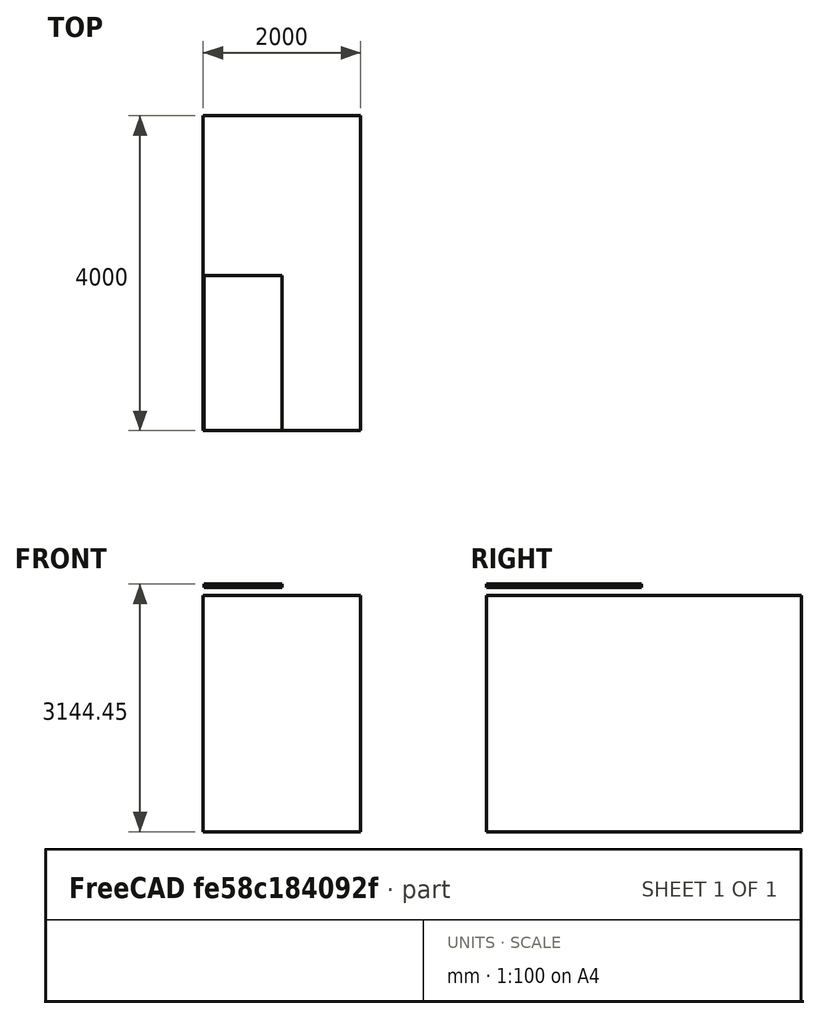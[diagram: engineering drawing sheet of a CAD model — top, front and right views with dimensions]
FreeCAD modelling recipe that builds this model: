
FCSTD DOCUMENT  (FreeCAD 0.19R)
Label: genesis-booth
License: Creative Commons Attribution-ShareAlike
LicenseURL: http://creativecommons.org/licenses/by-sa/4.0/
objects: Sketcher::SketchObject×6, Part::Part2DObjectPython×6, Part::Fuse×2, Spreadsheet::Sheet×1, Part::Feature×1, Part::FeaturePython×1, Part::Extrusion×1, App::DocumentObjectGroup×1
note: 16 computed .brp shape members not serialized (recipe doc carries the construction recipe); baked Part::Feature solids carry a one-line shape summary decoded from their .brp

FEATURE [Sketcher::SketchObject] Sketch  label="exterior walls sketch"
  FullyConstrained = true
  expr: Constraints[7] = Spreadsheet.building_length
  expr: Constraints[6] = Spreadsheet.building_width
  sketch-geometry (4):
    g0: LineSegment StartX=1000 StartY=2000 StartZ=0 EndX=1000 EndY=-2000 EndZ=0
    g1: LineSegment StartX=1000 StartY=-2000 StartZ=0 EndX=-1000 EndY=-2000 EndZ=0
    g2: LineSegment StartX=-1000 StartY=-2000 StartZ=0 EndX=-1000 EndY=2000 EndZ=0
    g3: LineSegment StartX=-1000 StartY=2000 StartZ=0 EndX=1000 EndY=2000 EndZ=0
  constraints (10):
    c: Coincident(g0,g1)
    c: Coincident(g1,g2)
    c: Coincident(g2,g3)
    c: Coincident(g0,g3)
    c: Vertical(g0)
    c: Horizontal(g1)
    c: Distance(g3) = 2000
    c: Distance(g0) = 4000
    c: Symmetric(g2,g1,g-1)
    c: Symmetric(g2,g0,g-2)
FEATURE [Sketcher::SketchObject] Sketch001  label="roof sketch"
  AttachmentOffset = pos=(0,0,3000) rot=(0,0,1;0rad)
  ExternalGeometry = -> [Sketch]
  FullyConstrained = true
  MapMode = 2
  Placement = pos=(0,0,3000) rot=(0,0,1;0rad)
  Support = -> [Sketch]
  expr: .AttachmentOffset.Base.z = Spreadsheet.building_height
  sketch-geometry (5):
    g0: LineSegment StartX=1000 StartY=2000 StartZ=0 EndX=1000 EndY=-2000 EndZ=0
    g1: LineSegment StartX=1000 StartY=-2000 StartZ=0 EndX=-1000 EndY=-2000 EndZ=0
    g2: LineSegment StartX=-1000 StartY=-2000 StartZ=0 EndX=-1000 EndY=2000 EndZ=0
    g3: LineSegment StartX=-1000 StartY=2000 StartZ=0 EndX=1000 EndY=2000 EndZ=0
    g4: LineSegment StartX=0 StartY=2000 StartZ=0 EndX=0 EndY=-2000 EndZ=0
  constraints (12):
    c: Coincident(g-6,g0)
    c: Coincident(g0,g-4)
    c: Coincident(g0,g1)
    c: Coincident(g1,g-5)
    c: Coincident(g1,g2)
    c: Coincident(g2,g-6)
    c: Coincident(g2,g3)
    c: Coincident(g3,g0)
    c: Vertical(g4)
    c: PointOnObject(g4,g-2)
    c: PointOnObject(g4,g3)
    c: PointOnObject(g4,g1)
FEATURE [Spreadsheet::Sheet] Spreadsheet
  cells = B1=Length; C1=Width; D1=Height; A2=Exterior Walls; B2(building_length)==4m; C2(building_width)==2m; D2(building_height)==3m; A3=Roof; C3(roof_overhang)==8m; D3(roof_height)==0.1m; A4=Roof Overhang; D4(roof_overhang_loss)==1.5m
FEATURE [Sketcher::SketchObject] Sketch002  label="roof ridge sketch"
  AttachmentOffset = pos=(0,0,100) rot=(0,0,1;0rad)
  ExternalGeometry = -> [Sketch001]
  FullyConstrained = true
  MapMode = 2
  Placement = pos=(0,0,3100) rot=(0,0,1;0rad)
  Support = -> [Sketch001]
  expr: .AttachmentOffset.Base.z = Spreadsheet.roof_height + 0m
  sketch-geometry (3):
    g0: LineSegment StartX=0 StartY=2000 StartZ=0 EndX=0 EndY=-2000 EndZ=0
    g1: LineSegment StartX=0 StartY=2000 StartZ=0 EndX=0 EndY=2500 EndZ=0
    g2: LineSegment StartX=0 StartY=-2000 StartZ=0 EndX=0 EndY=-2500 EndZ=0
  constraints (8):
    c: Coincident(g-3,g0)
    c: Coincident(g0,g-3)
    c: Coincident(g1,g0)
    c: PointOnObject(g1,g-2)
    c: Coincident(g2,g0)
    c: PointOnObject(g2,g-2)
    c: Distance(g1) = 500
    c: Equal(g1,g2)
FEATURE [Part::Part2DObjectPython] Wire001  # Draft 2D object (typed FeaturePython)
  Area = 4.01995e+06
  ChamferSize = 0
  Closed = true
  End = (4.4338e-12,2000,3100)
  FilletRadius = 0
  Length = 10010
  MakeFace = true
  Placement = pos=(-1000,2000,3000) rot=(0.754466,0.044251,0.654846;1.70074rad)
  Points = (4) [(0,0,0),(-2748.15,509.448,2861.49),(-2183.33,-24.0816,3498.93),(564.82,-533.53,637.436)]
  Start = (-1000,2000,3000)
  Subdivisions = 0
FEATURE [Part::Part2DObjectPython] Wire002  # Draft 2D object (typed FeaturePython)
  Area = 4.01995e+06
  ChamferSize = 0
  Closed = true
  End = (-4.3201e-12,2000,3100)
  FilletRadius = 0
  Length = 10010
  MakeFace = true
  Placement = pos=(0,-2000,3100) rot=(0.754466,0.044251,0.654846;1.70074rad)
  Points = (4) [(0,0,0),(461.981,-689.697,566.473),(3210.13,-1199.15,-2295.02),(2748.15,-509.448,-2861.49)]
  Start = (0,-2000,3100)
  Subdivisions = 0
FEATURE [Part::Fuse] Fusion  label="rooftop"
  Base = -> Wire002
  Tool = -> Wire001
FEATURE [Part::Feature] Part__Feature  label="PV Panel"
  Placement = pos=(-2293.4,-2787.4,-3250) rot=(0,0,1;0rad)
  shape: bbox 990.6 x 1969 x 44.45 mm, 6 faces (baked)
FEATURE [Part::FeaturePython] Array  label="PV Array"  # Draft array (typed FeaturePython)
  Angle = 360
  ArrayType = 0
  Axis = (0,0,1)
  Base = -> Part__Feature
  Center = (0,0,0)
  Count = 4
  ExpandArray = false
  Fuse = false
  IntervalAxis = (0,0,0)
  IntervalX = (1000,0,0)
  IntervalY = (0,2000,0)
  IntervalZ = (0,0,100)
  NumberCircles = 3
  NumberPolar = 5
  NumberX = 2
  NumberY = 2
  NumberZ = 1
  PlacementList = 4 placements: [(-2293.4,-2787.4,-3250),(-2293.4,-787.4,-3250),(-1293.4,-2787.4,-3250),(-1293.4,-787.4,-3250)]
  RadialDistance = 50
  ScaleList = (4) [(1,1,1),(1,1,1),(1,1,1),(1,1,1)]
  Symmetry = 1
  TangentialDistance = 25
FEATURE [Part::Extrusion] Extrude  label="Exterior Walls"
  Base = -> Sketch
  Dir = (0,0,1)
  DirMode = 2
  FaceMakerClass = Part::FaceMakerBullseye
  LengthFwd = 3000
  LengthRev = 0
  Solid = true
  Symmetric = false
  expr: LengthFwd = Spreadsheet.building_height
FEATURE [Sketcher::SketchObject] Sketch003  label="roof overhang sketch"
  ExternalGeometry = -> [Sketch001]
  FullyConstrained = true
  Placement = pos=(0,0,1500) rot=(0,0,1;0rad)
  expr: .Placement.Base.z = Spreadsheet.building_height - Spreadsheet.roof_overhang_loss
  expr: Constraints[14] = Spreadsheet.roof_overhang
  expr: Constraints[7] = Spreadsheet.roof_overhang
  sketch-geometry (6):
    g0: LineSegment StartX=-1000 StartY=2000 StartZ=0 EndX=-9000 EndY=2000 EndZ=0
    g1: LineSegment StartX=-9000 StartY=2000 StartZ=0 EndX=-9000 EndY=-2000 EndZ=0
    g2: LineSegment StartX=-9000 StartY=-2000 StartZ=0 EndX=-1000 EndY=-2000 EndZ=0
    g3: LineSegment StartX=1000 StartY=2000 StartZ=0 EndX=9000 EndY=2000 EndZ=0
    g4: LineSegment StartX=9000 StartY=2000 StartZ=0 EndX=9000 EndY=-2000 EndZ=0
    g5: LineSegment StartX=9000 StartY=-2000 StartZ=0 EndX=1000 EndY=-2000 EndZ=0
  constraints (16):
    c: Coincident(g-3,g0)
    c: Horizontal(g0)
    c: Coincident(g0,g1)
    c: Vertical(g1)
    c: Coincident(g1,g2)
    c: Coincident(g2,g-3)
    c: Horizontal(g2)
    c: Distance(g0) = 8000
    c: Coincident(g-4,g3)
    c: Horizontal(g3)
    c: Coincident(g3,g4)
    c: Coincident(g4,g5)
    c: Coincident(g5,g-4)
    c: Horizontal(g5)
    c: Distance(g3) = 8000
    c: Vertical(g4)
FEATURE [Part::Part2DObjectPython] Wire  label="left roof overhang"  # Draft 2D object (typed FeaturePython)
  Area = 3.25576e+07
  ChamferSize = 0
  Closed = true
  End = (-1000,2000,3000)
  FilletRadius = 0
  Length = 24278.8
  MakeFace = true
  Placement = pos=(-1000,-2000,3000) rot=(0.966472,-0.227442,0.119173;1.39842rad)
  Points = (4) [(0,0,0),(-8042.26,1001.61,754.259),(-8301.08,1859.14,-3144.16),(-258.821,857.528,-3898.42)]
  Start = (-1000,-2000,3000)
  Subdivisions = 0
FEATURE [Part::Part2DObjectPython] Wire003  label="right roof overhang"  # Draft 2D object (typed FeaturePython)
  Area = 3.25576e+07
  ChamferSize = 0
  Closed = true
  End = (1000,-2000,3000)
  FilletRadius = 0
  Length = 24278.8
  MakeFace = true
  Placement = pos=(1000,2000,3000) rot=(0.978165,-0.102065,0.18104;1.276rad)
  Points = (4) [(0,0,0),(7419.9,-3336.77,-246.908),(7010.3,-4528.5,3549.41),(-409.6,-1191.73,3796.31)]
  Start = (1000,2000,3000)
  Subdivisions = 0
FEATURE [Sketcher::SketchObject] Sketch004  label="footprint"
  ExternalGeometry = -> [Sketch003]
  FullyConstrained = true
  sketch-geometry (10):
    g0: LineSegment StartX=-1000 StartY=2000 StartZ=0 EndX=-9000 EndY=2000 EndZ=0
    g1: LineSegment StartX=-9000 StartY=2000 StartZ=0 EndX=-9000 EndY=-2000 EndZ=0
    g2: LineSegment StartX=-9000 StartY=-2000 StartZ=0 EndX=-1000 EndY=-2000 EndZ=0
    g3: LineSegment StartX=-8000 StartY=2000 StartZ=0 EndX=-8000 EndY=-2000 EndZ=0
    g4: LineSegment StartX=-7000 StartY=2000 StartZ=0 EndX=-7000 EndY=-2000 EndZ=0
    g5: LineSegment StartX=-6000 StartY=2000 StartZ=0 EndX=-6000 EndY=-2000 EndZ=0
    g6: LineSegment StartX=-5000 StartY=2000 StartZ=0 EndX=-5000 EndY=-2000 EndZ=0
    g7: LineSegment StartX=-4000 StartY=2000 StartZ=0 EndX=-4000 EndY=-2000 EndZ=0
    g8: LineSegment StartX=-3000 StartY=2000 StartZ=0 EndX=-3000 EndY=-2000 EndZ=0
    g9: LineSegment StartX=-2000 StartY=2000 StartZ=0 EndX=-2000 EndY=-2000 EndZ=0
  constraints (34):
    c: PointOnObject(g3,g-4)
    c: DistanceX(g-5,g3) = 1000
    c: Coincident(g-4,g0)
    c: Coincident(g0,g-5)
    c: Coincident(g0,g1)
    c: Coincident(g1,g-6)
    c: Coincident(g1,g2)
    c: Coincident(g2,g-6)
    c: PointOnObject(g3,g2)
    c: Vertical(g3)
    c: PointOnObject(g4,g0)
    c: PointOnObject(g4,g2)
    c: Vertical(g4)
    c: PointOnObject(g5,g0)
    c: PointOnObject(g5,g2)
    c: Vertical(g5)
    c: PointOnObject(g6,g0)
    c: PointOnObject(g6,g2)
    c: Vertical(g6)
    c: PointOnObject(g7,g0)
    c: PointOnObject(g7,g2)
    c: PointOnObject(g8,g0)
    c: PointOnObject(g8,g2)
    c: Vertical(g8)
    c: PointOnObject(g9,g0)
    c: PointOnObject(g9,g2)
    c: Vertical(g9)
    c: Vertical(g7)
    c: Distance(g3,g4) = 1000
    c: Distance(g4,g5) = 1000
    c: Distance(g5,g6) = 1000
    c: Distance(g6,g7) = 1000
    c: Distance(g7,g8) = 1000
    c: Distance(g9,g8) = 1000
FEATURE [Sketcher::SketchObject] Sketch005  label="roof small overhang sketch"
  ExternalGeometry = -> [Sketch001]
  FullyConstrained = true
  Placement = pos=(0,0,3000) rot=(0,0,1;0rad)
  expr: .Placement.Base.z = Spreadsheet.building_height
  sketch-geometry (4):
    g0: LineSegment StartX=1000 StartY=2000 StartZ=0 EndX=1000 EndY=2500 EndZ=0
    g1: LineSegment StartX=-1000 StartY=2000 StartZ=0 EndX=-1000 EndY=2500 EndZ=0
    g2: LineSegment StartX=-1000 StartY=-2000 StartZ=0 EndX=-1000 EndY=-2500 EndZ=0
    g3: LineSegment StartX=1000 StartY=-2000 StartZ=0 EndX=1000 EndY=-2500 EndZ=0
  constraints (12):
    c: Coincident(g-4,g0)
    c: Coincident(g-6,g1)
    c: Vertical(g1)
    c: Vertical(g2)
    c: Coincident(g-5,g3)
    c: Vertical(g3)
    c: Vertical(g0)
    c: Distance(g1) = 500
    c: Equal(g1,g0)
    c: Equal(g0,g2)
    c: Equal(g2,g3)
    c: Coincident(g2,g-6)
FEATURE [Part::Part2DObjectPython] Wire004  # Draft 2D object (typed FeaturePython)
  Area = 5.02494e+06
  ChamferSize = 0
  Closed = true
  End = (0,2500,3100)
  FilletRadius = 0
  Length = 12010
  MakeFace = true
  Placement = pos=(0,-2500,3100) rot=(0.788402,-0.57734,0.21237;1.22076rad)
  Points = (5) [(0,0,0),(-816.585,432.571,395.058),(-1264.74,2961.33,-3300.15),(-1314.53,3242.3,-3710.73),(-497.948,2809.73,-4105.78)]
  Start = (0,-2500,3100)
  Subdivisions = 0
FEATURE [Part::Part2DObjectPython] Wire005  # Draft 2D object (typed FeaturePython)
  Area = 5.02494e+06
  ChamferSize = 0
  Closed = true
  End = (2.274e-13,-2500,3100)
  FilletRadius = 0
  Length = 12010
  MakeFace = true
  Placement = pos=(-1.3642e-12,2500,3100) rot=(0.735403,-0.462369,0.495377;1.1552rad)
  Points = (4) [(0,0,0),(662.181,-709.579,-260.795),(-590.127,-3365.61,3786.09),(-1252.31,-2656.03,4046.88)]
  Start = (-1.3642e-12,2500,3100)
  Subdivisions = 0
FEATURE [Part::Fuse] Fusion001  label="rooftop w overhang"
  Base = -> Wire004
  Tool = -> Wire005
FEATURE [App::DocumentObjectGroup] Group  label="roof"
  Group = -> [Fusion,Array,Sketch003,Wire,Wire003,Sketch001,Sketch002,Fusion001,Sketch005]
